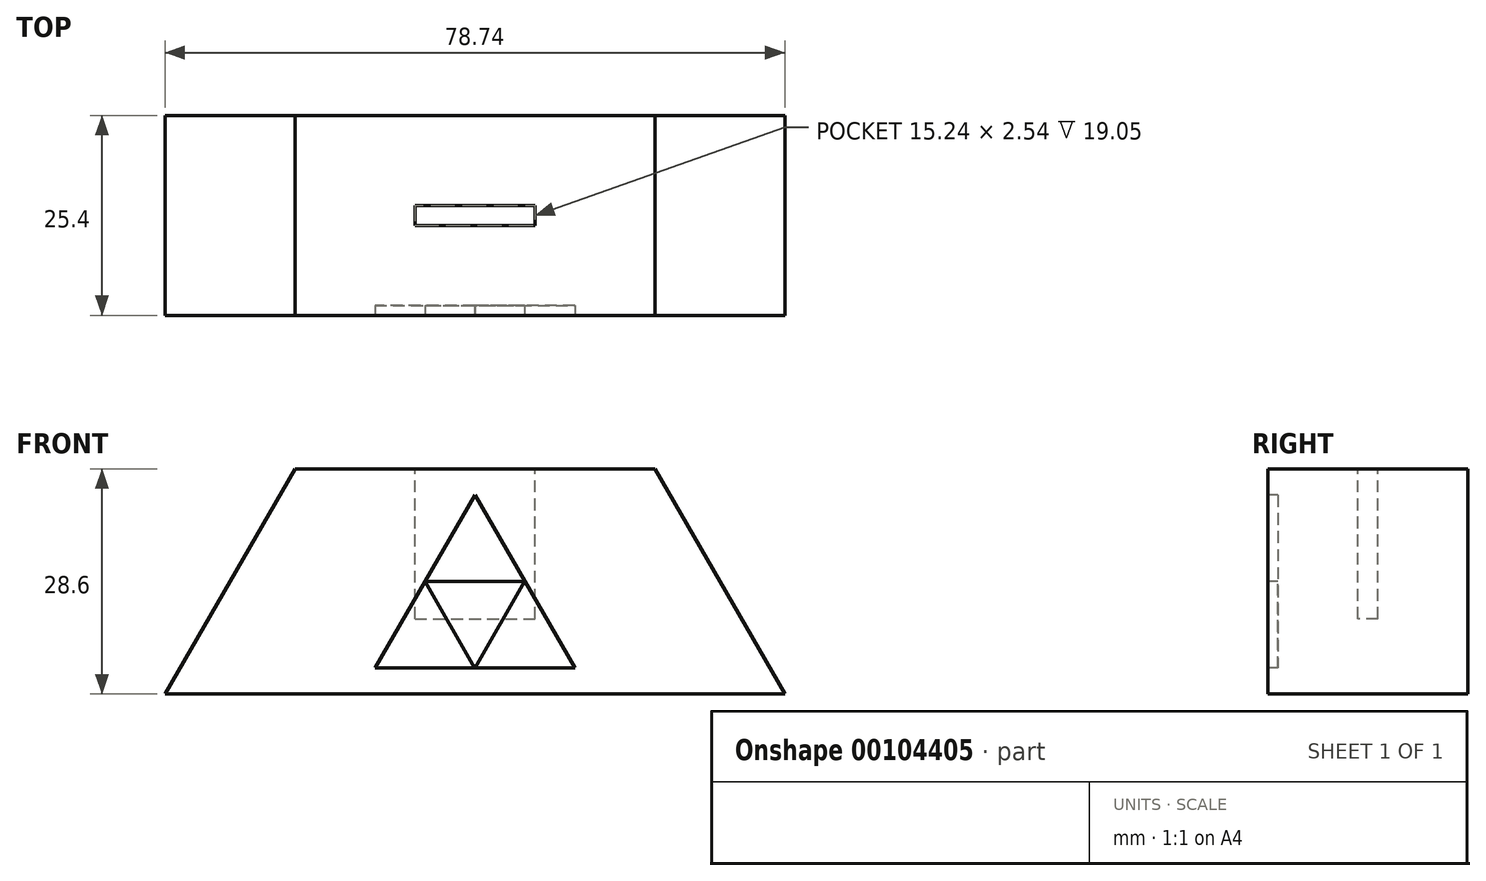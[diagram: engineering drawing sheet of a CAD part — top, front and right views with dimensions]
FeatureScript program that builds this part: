
annotation { "Feature Type Name" : "Feature", "Feature Type Description" : "" }
export const myFeature = defineFeature(function(context is Context, id is Id, definition is map)
    precondition{}
    {
        {
            var Q0;
            Q0=qCreatedBy(makeId("Front.planeOp"),FACE);
            var sketch = newSketch(context, id + "F0", { "sketchPlane" : qUnion([Q0])});
            skLineSegment(sketch, "E0", {"start": v(-39.37, -14.3) * mm, "end": v(-22.86, 14.3) * mm});
            skLineSegment(sketch, "E1", {"start": v(-22.86, 14.3) * mm, "end": v(22.86, 14.3) * mm});
            skLineSegment(sketch, "E2", {"start": v(22.86, 14.3) * mm, "end": v(39.37, -14.3) * mm});
            skLineSegment(sketch, "E3", {"start": v(39.37, -14.3) * mm, "end": v(-39.37, -14.3) * mm});
            skLineSegment(sketch, "E4", {"start": v(0, 14.3) * mm, "end": v(0, -14.3) * mm});
            skPoint(sketch, "E5", {"position": v(0, 0) * mm});
            skLineSegment(sketch, "E6", {"start": v(-31.12, 0) * mm, "end": v(31.12, 0) * mm});
            skSolve(sketch);
        }
        {
            var Q0;
            {var subQ0=sQuery(id+"F0.wireOp",EDGE,"E1");var subQ1=sQuery(id+"F0.wireOp",EDGE,"E0");var subQ2=makeQuery(id+"F0.imprint","INTERSECT",VERTEX,{"derivedFrom":[subQ1,subQ0]});Q0=makeQuery(id+"F0.imprint","IMPRINT",FACE,{"disambiguationData":[TD([[makeQuery(id+"F0.imprint","IMPRINT",EDGE,{"disambiguationData":[TD([[subQ2,1.0]])],"derivedFrom":subQ1}),-1.0]])]});}
            var Q1;
            {var subQ0=sQuery(id+"F0.wireOp",EDGE,"E2");var subQ1=sQuery(id+"F0.wireOp",EDGE,"E1");var subQ2=makeQuery(id+"F0.imprint","INTERSECT",VERTEX,{"derivedFrom":[subQ1,subQ0]});Q1=makeQuery(id+"F0.imprint","IMPRINT",FACE,{"disambiguationData":[TD([[makeQuery(id+"F0.imprint","IMPRINT",EDGE,{"disambiguationData":[TD([[subQ2,1.0]])],"derivedFrom":subQ1}),-1.0]])]});}
            var Q2;
            {var subQ0=sQuery(id+"F0.wireOp",EDGE,"E3");var subQ1=sQuery(id+"F0.wireOp",EDGE,"E2");var subQ2=makeQuery(id+"F0.imprint","INTERSECT",VERTEX,{"derivedFrom":[subQ1,subQ0]});Q2=makeQuery(id+"F0.imprint","IMPRINT",FACE,{"disambiguationData":[TD([[makeQuery(id+"F0.imprint","IMPRINT",EDGE,{"disambiguationData":[TD([[subQ2,1.0]])],"derivedFrom":subQ1}),-1.0]])]});}
            var Q3;
            {var subQ0=sQuery(id+"F0.wireOp",EDGE,"E3");var subQ1=sQuery(id+"F0.wireOp",EDGE,"E0");var subQ2=makeQuery(id+"F0.imprint","INTERSECT",VERTEX,{"derivedFrom":[subQ1,subQ0]});Q3=makeQuery(id+"F0.imprint","IMPRINT",FACE,{"disambiguationData":[TD([[makeQuery(id+"F0.imprint","IMPRINT",EDGE,{"disambiguationData":[TD([[subQ2,-1.0]])],"derivedFrom":subQ1}),-1.0]])]});}
            extrude(context, id + "F1", {"entities" : qUnion([Q0, Q1, Q2, Q3]), "endBound" : BoundingType.SYMMETRIC, "depth" : 25.4 * mm});
        }
        {
            var Q0;
            Q0=makeQuery(id+"F1.opExtrude","CAP_FACE",FACE,{"disambiguationData":[OSD([sQuery(id+"F0.wireOp",EDGE,"E0"),sQuery(id+"F0.wireOp",EDGE,"E1"),sQuery(id+"F0.wireOp",EDGE,"E2"),sQuery(id+"F0.wireOp",EDGE,"E3")])],"isStart":false});
            var sketch = newSketch(context, id + "F2", { "sketchPlane" : qUnion([Q0])});
            skLineSegment(sketch, "E7", {"start": v(0, 11) * mm, "end": v(-12.7, -11) * mm});
            skLineSegment(sketch, "E8", {"start": v(-12.7, -11) * mm, "end": v(12.7, -11) * mm});
            skLineSegment(sketch, "E9", {"start": v(12.7, -11) * mm, "end": v(0, 11) * mm});
            skLineSegment(sketch, "E10", {"start": v(-6.35, 0) * mm, "end": v(6.35, 0) * mm});
            skLineSegment(sketch, "E11", {"start": v(6.35, 0) * mm, "end": v(0, -11) * mm});
            skLineSegment(sketch, "E12", {"start": v(0, -11) * mm, "end": v(-6.35, 0) * mm});
            skArc(sketch, "E13", {"start": v(-6.35, 0) * mm, "mid": v(-6.35, 0) * mm, "end": v(-6.35, 0) * mm});
            skArc(sketch, "E14", {"start": v(0, -11) * mm, "mid": v(0, -11) * mm, "end": v(0, -11) * mm});
            skArc(sketch, "E15", {"start": v(6.35, 0) * mm, "mid": v(6.35, 0) * mm, "end": v(6.35, 0) * mm});
            skSolve(sketch);
        }
        {
            var Q0;
            {var subQ3=sQuery(id+"F2.wireOp",EDGE,"E12");Q0=makeQuery(id+"F2.imprint","IMPRINT",FACE,{"disambiguationData":[TD([[makeQuery(id+"F2.imprint","IMPRINT",EDGE,{"derivedFrom":subQ3}),1.0]])]});}
            extrude(context, id + "F3", {"entities" : qUnion([Q0]), "operationType" : NewBodyOperationType.REMOVE, "oppositeDirection" : true, "depth" : 1.27 * mm});
        }
        {
            var Q0;
            {var subQ1=sQuery(id+"F2.wireOp",EDGE,"E7");var subQ7=sQuery(id+"F2.wireOp",EDGE,"E9");var subQ8=makeQuery(id+"F2.imprint","INTERSECT",VERTEX,{"derivedFrom":[subQ1,subQ7]});Q0=makeQuery(id+"F2.imprint","IMPRINT",FACE,{"disambiguationData":[TD([[makeQuery(id+"F2.imprint","IMPRINT",EDGE,{"disambiguationData":[TD([[subQ8,-1.0]])],"derivedFrom":subQ1}),1.0]])]});}
            var Q1;
            {var subQ1=sQuery(id+"F2.wireOp",EDGE,"E7");var subQ7=sQuery(id+"F2.wireOp",EDGE,"E8");var subQ8=makeQuery(id+"F2.imprint","INTERSECT",VERTEX,{"derivedFrom":[subQ1,subQ7]});Q1=makeQuery(id+"F2.imprint","IMPRINT",FACE,{"disambiguationData":[TD([[makeQuery(id+"F2.imprint","IMPRINT",EDGE,{"disambiguationData":[TD([[subQ8,1.0]])],"derivedFrom":subQ1}),1.0]])]});}
            var Q2;
            {var subQ1=sQuery(id+"F2.wireOp",EDGE,"E8");var subQ7=sQuery(id+"F2.wireOp",EDGE,"E9");var subQ8=makeQuery(id+"F2.imprint","INTERSECT",VERTEX,{"derivedFrom":[subQ1,subQ7]});Q2=makeQuery(id+"F2.imprint","IMPRINT",FACE,{"disambiguationData":[TD([[makeQuery(id+"F2.imprint","IMPRINT",EDGE,{"disambiguationData":[TD([[subQ8,1.0]])],"derivedFrom":subQ1}),1.0]])]});}
            var Q3;
            {var subQ1=sQuery(id+"F2.wireOp",EDGE,"E7");var subQ3=sQuery(id+"F2.wireOp",EDGE,"E13");var subQ4=makeQuery(id+"F2.imprint","INTERSECT",VERTEX,{"disambiguationData":[OD(1.0)],"derivedFrom":[subQ1,subQ3]});Q3=makeQuery(id+"F2.imprint","IMPRINT",FACE,{"disambiguationData":[TD([[makeQuery(id+"F2.imprint","IMPRINT",EDGE,{"disambiguationData":[TD([[subQ4,1.0]])],"derivedFrom":subQ3}),1.0]])]});}
            var Q4;
            {var subQ1=sQuery(id+"F2.wireOp",EDGE,"E10");var subQ3=sQuery(id+"F2.wireOp",EDGE,"E13");var subQ4=makeQuery(id+"F2.imprint","INTERSECT",VERTEX,{"derivedFrom":[subQ1,subQ3]});Q4=makeQuery(id+"F2.imprint","IMPRINT",FACE,{"disambiguationData":[TD([[makeQuery(id+"F2.imprint","IMPRINT",EDGE,{"disambiguationData":[TD([[subQ4,1.0]])],"derivedFrom":subQ3}),1.0]])]});}
            var Q5;
            {var subQ1=sQuery(id+"F2.wireOp",EDGE,"E7");var subQ3=sQuery(id+"F2.wireOp",EDGE,"E13");var subQ4=makeQuery(id+"F2.imprint","INTERSECT",VERTEX,{"disambiguationData":[OD(0.0)],"derivedFrom":[subQ1,subQ3]});Q5=makeQuery(id+"F2.imprint","IMPRINT",FACE,{"disambiguationData":[TD([[makeQuery(id+"F2.imprint","IMPRINT",EDGE,{"disambiguationData":[TD([[subQ4,-1.0]])],"derivedFrom":subQ3}),1.0]])]});}
            var Q6;
            {var subQ1=sQuery(id+"F2.wireOp",EDGE,"E9");var subQ3=sQuery(id+"F2.wireOp",EDGE,"E15");var subQ4=makeQuery(id+"F2.imprint","INTERSECT",VERTEX,{"disambiguationData":[OD(1.0)],"derivedFrom":[subQ1,subQ3]});Q6=makeQuery(id+"F2.imprint","IMPRINT",FACE,{"disambiguationData":[TD([[makeQuery(id+"F2.imprint","IMPRINT",EDGE,{"disambiguationData":[TD([[subQ4,1.0]])],"derivedFrom":subQ3}),1.0]])]});}
            var Q7;
            {var subQ1=sQuery(id+"F2.wireOp",EDGE,"E10");var subQ3=sQuery(id+"F2.wireOp",EDGE,"E15");var subQ4=makeQuery(id+"F2.imprint","INTERSECT",VERTEX,{"derivedFrom":[subQ1,subQ3]});Q7=makeQuery(id+"F2.imprint","IMPRINT",FACE,{"disambiguationData":[TD([[makeQuery(id+"F2.imprint","IMPRINT",EDGE,{"disambiguationData":[TD([[subQ4,-1.0]])],"derivedFrom":subQ3}),1.0]])]});}
            var Q8;
            {var subQ1=sQuery(id+"F2.wireOp",EDGE,"E9");var subQ3=sQuery(id+"F2.wireOp",EDGE,"E15");var subQ4=makeQuery(id+"F2.imprint","INTERSECT",VERTEX,{"disambiguationData":[OD(0.0)],"derivedFrom":[subQ1,subQ3]});Q8=makeQuery(id+"F2.imprint","IMPRINT",FACE,{"disambiguationData":[TD([[makeQuery(id+"F2.imprint","IMPRINT",EDGE,{"disambiguationData":[TD([[subQ4,-1.0]])],"derivedFrom":subQ3}),1.0]])]});}
            var Q9;
            {var subQ1=sQuery(id+"F2.wireOp",EDGE,"E8");var subQ3=sQuery(id+"F2.wireOp",EDGE,"E14");var subQ4=makeQuery(id+"F2.imprint","INTERSECT",VERTEX,{"disambiguationData":[OD(0.0)],"derivedFrom":[subQ1,subQ3]});Q9=makeQuery(id+"F2.imprint","IMPRINT",FACE,{"disambiguationData":[TD([[makeQuery(id+"F2.imprint","IMPRINT",EDGE,{"disambiguationData":[TD([[subQ4,-1.0]])],"derivedFrom":subQ3}),1.0]])]});}
            var Q10;
            {var subQ1=sQuery(id+"F2.wireOp",EDGE,"E11");var subQ3=sQuery(id+"F2.wireOp",EDGE,"E14");var subQ4=makeQuery(id+"F2.imprint","INTERSECT",VERTEX,{"derivedFrom":[subQ1,subQ3]});Q10=makeQuery(id+"F2.imprint","IMPRINT",FACE,{"disambiguationData":[TD([[makeQuery(id+"F2.imprint","IMPRINT",EDGE,{"disambiguationData":[TD([[subQ4,-1.0]])],"derivedFrom":subQ3}),1.0]])]});}
            var Q11;
            {var subQ1=sQuery(id+"F2.wireOp",EDGE,"E8");var subQ3=sQuery(id+"F2.wireOp",EDGE,"E14");var subQ4=makeQuery(id+"F2.imprint","INTERSECT",VERTEX,{"disambiguationData":[OD(1.0)],"derivedFrom":[subQ1,subQ3]});Q11=makeQuery(id+"F2.imprint","IMPRINT",FACE,{"disambiguationData":[TD([[makeQuery(id+"F2.imprint","IMPRINT",EDGE,{"disambiguationData":[TD([[subQ4,1.0]])],"derivedFrom":subQ3}),1.0]])]});}
            extrude(context, id + "F4", {"entities" : qUnion([Q0, Q1, Q2, Q3, Q4, Q5, Q6, Q7, Q8, Q9, Q10, Q11]), "operationType" : NewBodyOperationType.REMOVE, "oppositeDirection" : true, "depth" : 1.27 * mm});
        }
        {
            var Q0;
            Q0=makeQuery(id+"F1.opExtrude","SWEPT_FACE",FACE,{"disambiguationData":[OSD([sQuery(id+"F0.wireOp",EDGE,"E1")])]});
            var sketch = newSketch(context, id + "F5", { "sketchPlane" : qUnion([Q0])});
            skLineSegment(sketch, "E16.bottom", {"start": v(-7.62, 1.27) * mm, "end": v(7.62, 1.27) * mm});
            skLineSegment(sketch, "E16.top", {"start": v(-7.62, -1.27) * mm, "end": v(7.62, -1.27) * mm});
            skLineSegment(sketch, "E16.left", {"start": v(-7.62, 1.27) * mm, "end": v(-7.62, -1.27) * mm});
            skLineSegment(sketch, "E16.right", {"start": v(7.62, 1.27) * mm, "end": v(7.62, -1.27) * mm});
            skPoint(sketch, "E16.middle", {"position": v(0, 0) * mm});
            skSolve(sketch);
        }
        {
            var Q0;
            Q0=makeQuery(id+"F5.imprint","IMPRINT",FACE,{"disambiguationData":[TD([[makeQuery(id+"F5.imprint","IMPRINT",EDGE,{"derivedFrom":sQuery(id+"F5.wireOp",EDGE,"E16.bottom")}),-1.0]])]});
            extrude(context, id + "F6", {"entities" : qUnion([Q0]), "operationType" : NewBodyOperationType.REMOVE, "oppositeDirection" : true, "depth" : 19.05 * mm});
        }
    });
